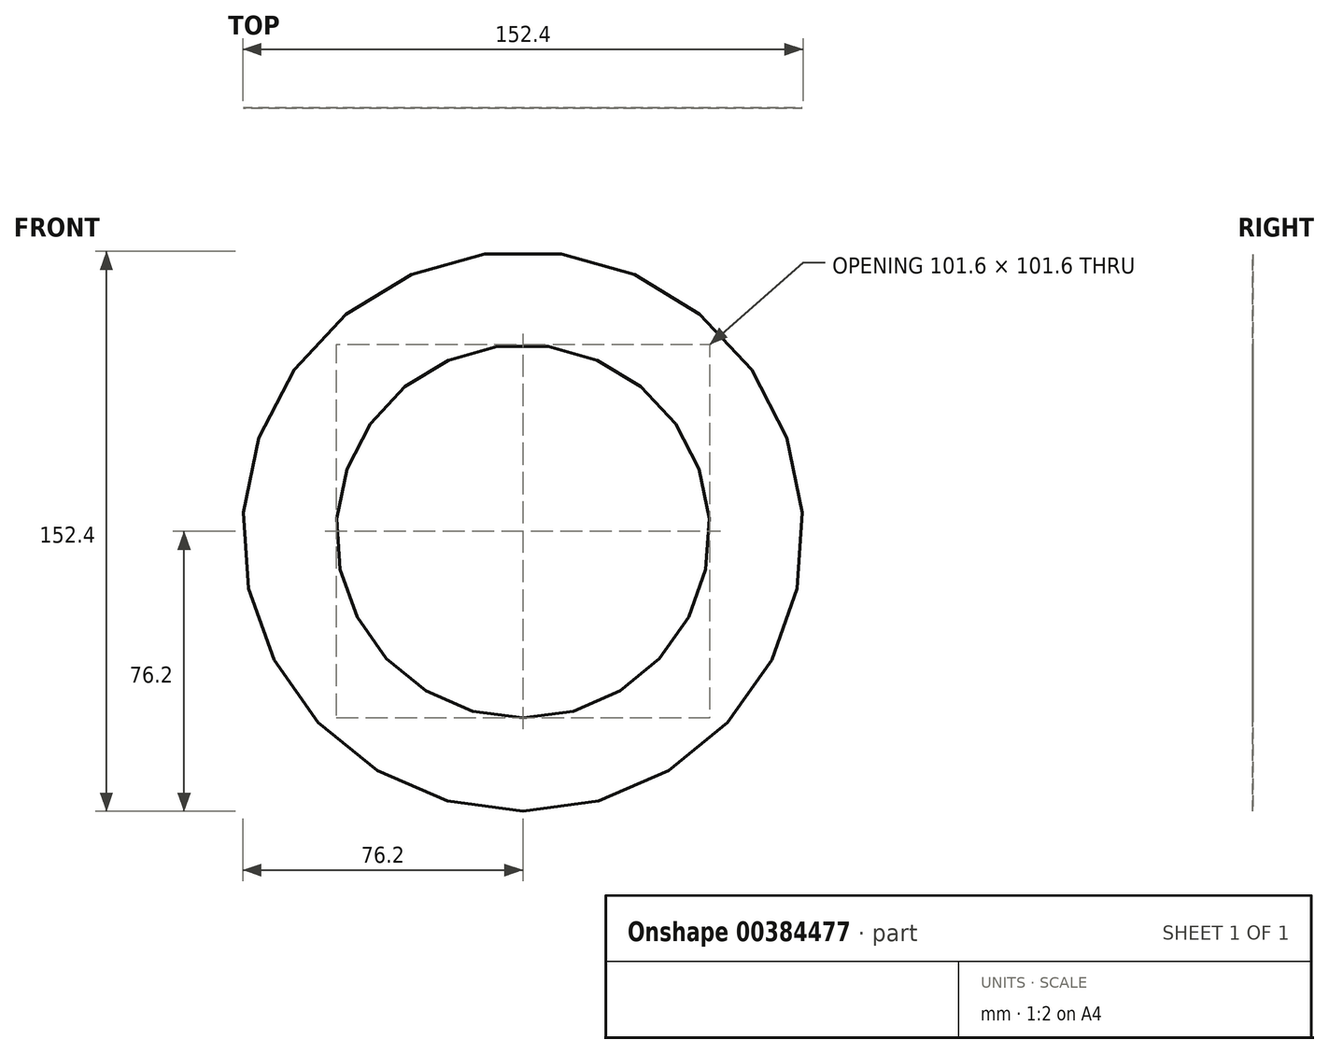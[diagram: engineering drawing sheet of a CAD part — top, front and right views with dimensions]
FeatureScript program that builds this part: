
annotation { "Feature Type Name" : "Feature", "Feature Type Description" : "" }
export const myFeature = defineFeature(function(context is Context, id is Id, definition is map)
    precondition{}
    {
        {
            var Q0;
            Q0=qCreatedBy(makeId("Front.planeOp"),FACE);
            var sketch = newSketch(context, id + "F0", { "sketchPlane" : qUnion([Q0])});
            skCircle(sketch, "E0", {"center": v(0, 0) * mm, "radius": 76.2 * mm});
            skSolve(sketch);
        }
        {
            var Q0;
            Q0 = qSketchRegion(id + "F0", true);
            extrude(context, id + "F1", {"entities" : qUnion([Q0]), "depth" : 50.8 * mm});
        }
        {
            var Q0;
            Q0=makeQuery(id+"F1.opExtrude","CAP_EDGE",EDGE,{"disambiguationData":[OSD([sQuery(id+"F0.wireOp",EDGE,"E0")])],"isStart":false});
            fillet(context, id + "F2", {"entities" : qUnion([Q0]), "radius" : 25.4 * mm, "tangentPropagation" : true, "allowEdgeOverflow" : false});
        }
        {
            var Q0;
            Q0=makeQuery(id+"F1.opExtrude","CAP_EDGE",EDGE,{"disambiguationData":[OSD([sQuery(id+"F0.wireOp",EDGE,"E0")])],"isStart":true});
            fillet(context, id + "F3", {"entities" : qUnion([Q0]), "radius" : 25.4 * mm, "tangentPropagation" : true, "allowEdgeOverflow" : false});
        }
        {
            var Q0;
            Q0=makeQuery(id+"F1.opExtrude","CAP_FACE",FACE,{"disambiguationData":[OSD([sQuery(id+"F0.wireOp",EDGE,"E0")])],"isStart":true});
            extrude(context, id + "F4", {"entities" : qUnion([Q0]), "operationType" : NewBodyOperationType.ADD, "depth" : 25.4 * mm});
        }
        {
            var Q0;
            Q0=makeQuery(id+"F4.opExtrude","CAP_FACE",FACE,{"disambiguationData":[OSD([sQuery(id+"F0.wireOp",EDGE,"E0")])],"isStart":false});
            var Q1;
            Q1=makeQuery(id+"F1.opExtrude","CAP_FACE",FACE,{"disambiguationData":[OSD([sQuery(id+"F0.wireOp",EDGE,"E0")])],"isStart":false});
            extrude(context, id + "F5", {"entities" : qUnion([Q0, Q1]), "operationType" : NewBodyOperationType.REMOVE, "oppositeDirection" : true, "depth" : 312.93 * mm});
        }
        {
            var Q0;
            {var subQ0=sQuery(id+"F0.wireOp",EDGE,"E0");Q0=makeQuery(id+"F4.boolean.opBoolean","MERGE",EDGE,{"derivedFrom":[makeQuery(id+"F3.opFillet","BLEND_EDGE",EDGE,{"blendedFrom":[makeQuery(id+"F1.opExtrude","CAP_EDGE",EDGE,{"disambiguationData":[OSD([subQ0])],"isStart":true}),makeQuery(id+"F1.opExtrude","CAP_FACE",FACE,{"disambiguationData":[OSD([subQ0])],"isStart":true})],"blendedInto":[makeQuery(id+"F1.opExtrude","CAP_FACE",FACE,{"disambiguationData":[OSD([subQ0])],"isStart":true})]}),makeQuery(id+"F4.opExtrude","CAP_EDGE",EDGE,{"disambiguationData":[OSD([subQ0])],"isStart":true})]});}
            var Q1;
            {var subQ0=sQuery(id+"F0.wireOp",EDGE,"E0");Q1=makeQuery(id+"F2.opFillet","BLEND_EDGE",EDGE,{"blendedFrom":[makeQuery(id+"F1.opExtrude","CAP_EDGE",EDGE,{"disambiguationData":[OSD([subQ0])],"isStart":false}),makeQuery(id+"F1.opExtrude","CAP_FACE",FACE,{"disambiguationData":[OSD([subQ0])],"isStart":false})],"blendedInto":[makeQuery(id+"F1.opExtrude","CAP_FACE",FACE,{"disambiguationData":[OSD([subQ0])],"isStart":false})]});}
            chamfer(context, id + "F6", {"entities" : qUnion([Q0, Q1]), "width" : 12.7 * mm, "tangentPropagation" : true});
        }
    });
